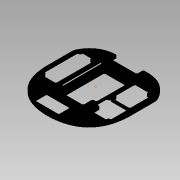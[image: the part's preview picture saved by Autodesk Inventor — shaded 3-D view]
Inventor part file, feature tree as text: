
AUTODESK INVENTOR PART (.ipt)
format: ipt  version: 2015 SP1 (Build 190203100, 203)  size: 584,192 bytes
history: native  units: mm
features: extrude x14, reference x10, sketch x8, fillet x4, projected_geometry x1
ambient origin geometry x8: Origin, YZ Plane, XZ Plane, XY Plane, X Axis, Y Axis, Z Axis, Center Point
bodies: Body1 (feature_tree)
feature tree (37):
  extrude  "Extrusion5"  Depth=75.0mm
  extrude  "Extrusion6"  Depth=65.0mm
  extrude  "Extrusion11"  Depth=130.0mm
  extrude  "Extrusion12"  Depth=40.0mm
  extrude  "Extrusion14"  Depth=4.0mm TaperAngle=0.0deg
  extrude  "Extrusion17"  Depth=48.26mm
  extrude  "Extrusion20"  Depth=48.26mm
  extrude  "Extrusion24"  Depth=2.0mm
  extrude  "Extrusion27"  Depth=10.0mm TaperAngle=0.0deg
  extrude  "Extrusion29"  Depth=3.0mm TaperAngle=0.0deg
  extrude  "Extrusion30"  Depth=2.0mm
  fillet  "Fillet1"  Radius=43.0mm
  extrude  "Extrusion31"  Depth=2.0mm
  fillet  "Fillet2"  Radius=85.0mm
  sketch  "Sketch25"  dims[d47=3.5mm d48=0.0mm d57=48.26mm]
  extrude  "Extrusion32"  Depth=2.0mm
  extrude  "Extrusion33"  Depth=2.0mm TaperAngle=0.0deg
  fillet  "Fillet3"  Radius=32.442mm
  fillet  "Fillet4"  Radius=32.442mm
  sketch  "Sketch7"  dims[d13=74.959789mm d14=75.0mm]
  sketch  "Sketch9"  dims[d15=65.0mm d16=65.0mm]
  reference  "Reference3"
  reference  "Reference4"
  reference  "Reference5"
  reference  "Reference6"
  reference  "Reference7"
  sketch  "Sketch13"  dims[d17=149.959789mm d18=130.0mm]
  reference  "Reference15"
  reference  "Reference16"
  reference  "Reference17"
  reference  "Reference18"
  reference  "Reference19"
  sketch  "Sketch18"  dims[d30=3.5mm d31=40.0mm]
  sketch  "Sketch24"  dims[d32=37.5mm d35=4.0mm d36=0.0mm]
  projected_geometry  "Projected Loop9"
  sketch  "Sketch26"  dims[d58=82.55mm d59=48.26mm]
  sketch  "Sketch27"  dims[d60=74.93mm d61=20.32mm d91=10.0mm d92=0.0mm d93=3.0mm d94=0.0mm d99=3.5mm d101=3.5mm d112=43.0mm d113=43.0mm d114=85.0mm d115=85.0mm d116=3.5mm d117=0.0mm d123=32.442mm d124=32.442mm d126=32.442mm d127=20.216mm d128=10.0mm d129=0.0mm d186=10.0mm d187=0.0mm d231=3.91262mm d274=10.0mm d275=0.0mm d294=5.842mm d311=5.0mm d312=5.0mm d313=5.0mm d314=5.0mm d315=10.0mm d316=0.0mm d317=20.825028mm d318=39.875028mm d319=1.332014mm d320=1.332014mm d321=1.332014mm d322=1.332014mm d323=10.412514mm d324=10.412514mm d325=1.332014mm d326=1.332014mm d327=1.332014mm d328=1.332014mm d329=1.332014mm d330=1.332014mm d331=1.332014mm d332=1.332014mm d333=4.662386mm d334=4.662386mm d335=5.510314mm d336=5.510314mm d337=4.662386mm d338=4.662386mm d339=5.510314mm d340=5.510314mm d348=2.0mm d364=2.0mm d370=180.0deg d379=90.0deg d380=90.0deg d381=2.0mm d382=0.0mm d383=10.0mm d384=0.0mm d385=1.0mm d387=3.5mm d388=3.5mm d389=3.5mm d390=3.5mm d391=3.5mm d393=3.5mm d394=2.0mm d395=3.5mm d396=3.5mm d397=2.0mm d398=10.0mm d399=0.0mm d400=10.0mm d401=2.0mm d402=2.0mm d403=3.5mm d404=0.0mm d407=0.0mm d408=180.0deg d409=2.0mm d410=3.0mm d411=0.0mm d412=2.0mm d413=35.0mm d414=1.555402mm d415=1.555402mm d416=10.0mm d417=0.0mm d418=4.0mm d419=4.0mm d420=0.0mm d421=3.0mm d422=2.0mm]
